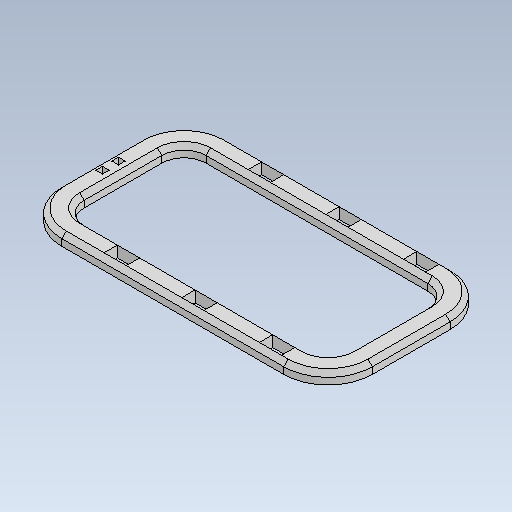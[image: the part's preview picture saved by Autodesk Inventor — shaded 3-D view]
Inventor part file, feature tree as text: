
AUTODESK INVENTOR PART (.ipt)
format: ipt  version: 2023 (Build 270158030, 158C)  size: 179,200 bytes
history: native  units: mm
features: reference x8, other x7, extrude x1, sketch x1
ambient origin geometry x8: Origin, YZ Plane, XZ Plane, XY Plane, X Axis, Y Axis, Z Axis, Center Point
bodies: Body1 (feature_tree)
feature tree (17):
  other  "baseplate"
  other  "V4.0-trebuchet-complete-parts.ipt"
  extrude  "Extrusion1"  TaperAngle=0.0deg  [1 undecoded]
  other  "baseplate::V4.0-trebuchet-complete-parts.ipt"
  other  "TaggingFeature1"
  sketch  "Sketch1"  dims[d0=10.0mm d1=0.0mm d2=0.0mm]
  reference  "Reference2"
  reference  "Reference3"
  reference  "Reference4"
  reference  "Reference5"
  reference  "Reference6"
  reference  "Reference7"
  reference  "Reference8"
  reference  "Reference9"
  other  "<userpath>\Documents\0004-inventor\3D-CAD-main\trebuchet\V4.0-trebuchet-printable.iam"
  other  "V4.0-trebuchet-printable.iam"
  other  "v4-latch:1"
note: 1 required parameter value undecoded (feature->parameter linkage not recoverable at this tier; creation-order binding heuristic only, values carry confidence <= 0.55)
